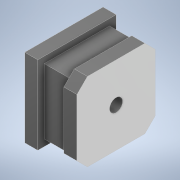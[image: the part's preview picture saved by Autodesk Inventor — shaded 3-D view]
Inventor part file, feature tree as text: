
AUTODESK INVENTOR PART (.ipt)
format: ipt  version: 2021 (Build 250183000, 183)  size: 126,464 bytes
history: native  units: mm
features: extrude x2, sketch x2, plane x1, chamfer x1
ambient origin geometry x8: Origin, YZ Plane, XZ Plane, XY Plane, X Axis, Y Axis, Z Axis, Center Point
bodies: Solid1 (feature_tree)
feature tree (6):
  extrude  "Extrusion1"  Depth=30.0mm
  plane  "Work Plane1"
  extrude  "Extrusion2"  Depth=20.0mm TaperAngle=0.0deg
  chamfer  "Chamfer1"  [1 undecoded]
  sketch  "Sketch1"  dims[d0=5.0mm d1=30.0mm]
  sketch  "Sketch2"  dims[d2=30.0mm d3=20.0mm d4=0.0mm d5=-5.0mm d6=25.0mm d7=25.0mm d8=10.0mm d9=0.0mm d10=4.0mm d11=2.0mm d12=45.0deg]
note: 1 required parameter value undecoded (feature->parameter linkage not recoverable at this tier; creation-order binding heuristic only, values carry confidence <= 0.55)
